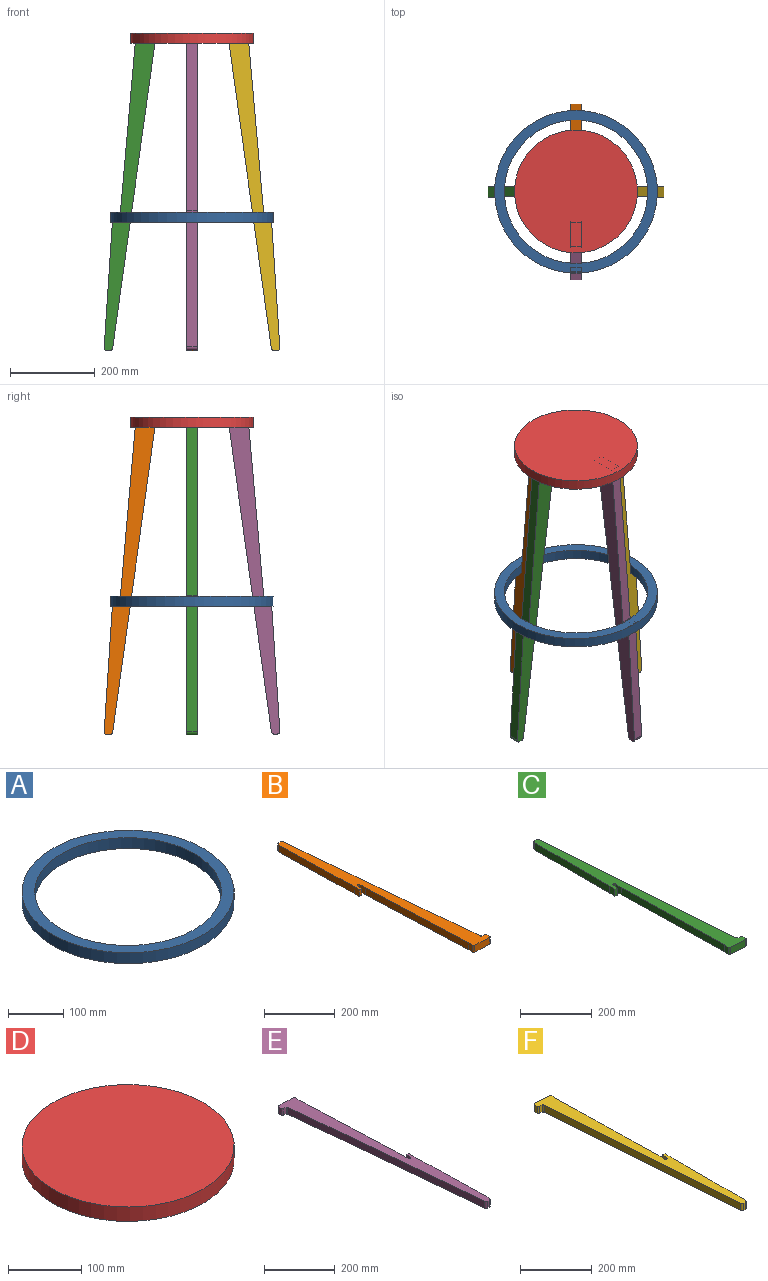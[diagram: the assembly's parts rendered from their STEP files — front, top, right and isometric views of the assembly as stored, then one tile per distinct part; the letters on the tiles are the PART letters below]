
ASSEMBLY  parts=6 mates=7
PART A: 40 faces, bbox 384x384x24 mm
  f0: plane 20x12.69mm, normal (-1,0,0), area 253.7mm2, adj f1,f31,f35,f36
  f1: cylinder r=4mm len=20mm, axis (0,0,-1), area 252.9mm2, adj f0,f2,f35,f36
  f2: plane 20x4.34mm, normal (0,1,0), area 86.9mm2, adj f1,f3,f35,f36
  f3: cylinder r=4mm len=20mm, axis (0,0,-1), area 251.3mm2, adj f2,f4,f35,f36
  f4: plane 20x8mm, normal (1,0,0), area 160mm2, adj f3,f5,f35,f36
  f5: cylinder r=4mm len=20mm, axis (0,0,-1), area 251.3mm2, adj f4,f6,f35,f36
  f6: plane 20x4.34mm, normal (0,-1,0), area 86.9mm2, adj f5,f31,f35,f36
  f7: plane 20x12.69mm, normal (0,-1,0), area 253.7mm2, adj f8,f28,f35,f39
  f8: cylinder r=4mm len=20mm, axis (0,0,-1), area 252.9mm2, adj f7,f9,f35,f39
  f9: plane 20x4.34mm, normal (-1,0,0), area 86.9mm2, adj f8,f10,f35,f39
  f10: cylinder r=4mm len=20mm, axis (0,0,-1), area 251.3mm2, adj f9,f11,f35,f39
  f11: plane 20x8mm, normal (0,1,0), area 160mm2, adj f10,f12,f35,f39
  f12: cylinder r=4mm len=20mm, axis (0,0,-1), area 251.3mm2, adj f11,f13,f35,f39
  f13: plane 20x4.34mm, normal (1,0,0), area 86.9mm2, adj f12,f28,f35,f39
  f14: plane 20x12.69mm, normal (0,1,0), area 253.7mm2, adj f15,f29,f35,f38
  f15: cylinder r=4mm len=20mm, axis (0,0,-1), area 252.9mm2, adj f14,f16,f35,f38
  f16: plane 20x4.34mm, normal (1,0,0), area 86.9mm2, adj f15,f17,f35,f38
  f17: cylinder r=4mm len=20mm, axis (0,0,-1), area 251.3mm2, adj f16,f18,f35,f38
  f18: plane 20x8mm, normal (0,-1,0), area 160mm2, adj f17,f19,f35,f38
  f19: cylinder r=4mm len=20mm, axis (0,0,-1), area 251.3mm2, adj f18,f20,f35,f38
  f20: plane 20x4.34mm, normal (-1,0,0), area 86.9mm2, adj f19,f29,f35,f38
  f21: plane 20x12.69mm, normal (1,0,0), area 253.7mm2, adj f22,f30,f35,f37
  f22: cylinder r=4mm len=20mm, axis (0,0,-1), area 252.9mm2, adj f21,f23,f35,f37
  f23: plane 20x4.34mm, normal (0,-1,0), area 86.9mm2, adj f22,f24,f35,f37
  f24: cylinder r=4mm len=20mm, axis (0,0,-1), area 251.3mm2, adj f23,f25,f35,f37
  f25: plane 20x8mm, normal (-1,0,0), area 160mm2, adj f24,f26,f35,f37
  f26: cylinder r=4mm len=20mm, axis (0,0,-1), area 251.3mm2, adj f25,f27,f35,f37
  f27: plane 20x4.34mm, normal (0,1,0), area 86.9mm2, adj f26,f30,f35,f37
  f28: cylinder r=4mm len=20mm, axis (0,0,-1), area 252.9mm2, adj f7,f13,f35,f39
  f29: cylinder r=4mm len=20mm, axis (0,0,-1), area 252.9mm2, adj f14,f20,f35,f38
  f30: cylinder r=4mm len=20mm, axis (0,0,-1), area 252.9mm2, adj f21,f27,f35,f37
  f31: cylinder r=4mm len=20mm, axis (0,0,-1), area 252.9mm2, adj f0,f6,f35,f36
  f32: cylinder r=169mm len=338mm, axis (0,0,-1), area 25484.6mm2, adj f34,f35
  f33: cylinder r=192mm len=384mm, axis (0,0,-1), area 28952.9mm2, adj f34,f35
  f34: plane 384x384mm, normal (0,0,1), area 26084.6mm2, adj f32,f33
  f35: plane 384x384mm, normal (0,0,-1), area 24847.9mm2, adj f0,f1,f2,f3,f4,f5,f6,f7
  f36: plane 26.4x15.2mm, normal (0,0,-1), area 309.2mm2, adj f0,f1,f2,f3,f4,f5,f6,f31
  f37: plane 26.4x15.2mm, normal (0,0,-1), area 309.2mm2, adj f21,f22,f23,f24,f25,f26,f27,f30
  f38: plane 26.4x15.2mm, normal (0,0,-1), area 309.2mm2, adj f14,f15,f16,f17,f18,f19,f20,f29
  f39: plane 26.4x15.2mm, normal (0,0,-1), area 309.2mm2, adj f7,f8,f9,f10,f11,f12,f13,f28
PART B: 21 faces, bbox 106.4x750.9x24 mm
  f0: plane 24x11.99mm, normal (1,-0.04,0), area 288mm2, adj f1,f18,f19,f20
  f1: cylinder r=4mm len=24mm, axis (0,0,-1), area 150.8mm2, adj f0,f2,f19,f20
  f2: plane 24x10.88mm, normal (0.04,1,0), area 261.3mm2, adj f1,f3,f19,f20
  f3: cylinder r=4mm len=24mm, axis (0,0,-1), area 137.6mm2, adj f2,f4,f19,f20
  f4: plane 720.18x67.82mm, normal (1,0.09,0), area 17360.9mm2, adj f3,f5,f19,f20
  f5: cylinder r=7mm len=24mm, axis (0,0,-1), area 240.7mm2, adj f4,f6,f19,f20
  f6: plane 24x6.09mm, normal (0.04,1,0), area 146.3mm2, adj f5,f7,f19,f20
  f7: cylinder r=7mm len=24mm, axis (0,0,-1), area 274.9mm2, adj f6,f8,f19,f20
  f8: plane 295.62x24mm, normal (-1,-0.02,0), area 7096.5mm2, adj f7,f9,f19,f20
  f9: plane 24x20.98mm, normal (-1,0.04,0), area 504mm2, adj f8,f10,f19,f20
  f10: plane 24x9.99mm, normal (-0.04,-1,0), area 240mm2, adj f9,f11,f19,f20
  f11: plane 24x16.98mm, normal (1,-0.04,0), area 408mm2, adj f10,f12,f19,f20
  f12: cylinder r=4.56mm len=24mm, axis (0,0,-1), area 343.8mm2, adj f11,f13,f19,f20
  f13: plane 24x21.98mm, normal (-1,0.04,0), area 528mm2, adj f12,f14,f19,f20
  f14: plane 398.63x24mm, normal (-1,-0.04,0), area 9576mm2, adj f13,f15,f19,f20
  f15: plane 24x15.98mm, normal (-1,0.04,0), area 384mm2, adj f14,f16,f19,f20
  f16: cylinder r=4mm len=24mm, axis (0,0,-1), area 150.8mm2, adj f15,f17,f19,f20
  f17: plane 56.95x24mm, normal (-0.04,-1,0), area 1368mm2, adj f16,f18,f19,f20
  f18: cylinder r=4mm len=24mm, axis (0,0,-1), area 150.8mm2, adj f0,f17,f19,f20
  f19: plane 750.88x106.39mm, normal (0,0,1), area 25896.7mm2, adj f0,f1,f2,f3,f4,f5,f6,f7
  f20: plane 750.88x106.39mm, normal (0,0,-1), area 25896.7mm2, adj f0,f1,f2,f3,f4,f5,f6,f7
PART C: 21 faces, bbox 92x752.8x24 mm
  f0: cylinder r=4mm len=24mm, axis (0,0,-1), area 150.8mm2, adj f1,f18,f19,f20
  f1: plane 24x10.86mm, normal (0.07,1,0), area 261.3mm2, adj f0,f2,f19,f20
  f2: cylinder r=4mm len=24mm, axis (0,0,-1), area 137.6mm2, adj f1,f3,f19,f20
  f3: plane 721.48x52.22mm, normal (1,0.07,0), area 17360.9mm2, adj f2,f4,f19,f20
  f4: cylinder r=7mm len=24mm, axis (0,0,-1), area 240.7mm2, adj f3,f5,f19,f20
  f5: plane 24x6.08mm, normal (0.07,1,0), area 146.3mm2, adj f4,f6,f19,f20
  f6: cylinder r=7mm len=24mm, axis (0,0,-1), area 274.9mm2, adj f5,f7,f19,f20
  f7: plane 295.69x24mm, normal (-1,0,0), area 7096.5mm2, adj f6,f8,f19,f20
  f8: plane 24x20.95mm, normal (-1,0.07,0), area 504mm2, adj f7,f9,f19,f20
  f9: plane 24x9.98mm, normal (-0.07,-1,0), area 240mm2, adj f8,f10,f19,f20
  f10: plane 24x16.96mm, normal (1,-0.07,0), area 408mm2, adj f9,f11,f19,f20
  f11: cylinder r=4.56mm len=24mm, axis (0,0,-1), area 343.8mm2, adj f10,f12,f19,f20
  f12: plane 24x21.95mm, normal (-1,0.07,0), area 528mm2, adj f11,f13,f19,f20
  f13: plane 398.91x24mm, normal (-1,-0.02,0), area 9576mm2, adj f12,f14,f19,f20
  f14: plane 24x15.97mm, normal (-1,0.07,0), area 384mm2, adj f13,f15,f19,f20
  f15: cylinder r=4mm len=24mm, axis (0,0,-1), area 150.8mm2, adj f14,f16,f19,f20
  f16: plane 56.88x24mm, normal (-0.07,-1,0), area 1368mm2, adj f15,f17,f19,f20
  f17: cylinder r=4mm len=24mm, axis (0,0,-1), area 150.8mm2, adj f16,f18,f19,f20
  f18: plane 24x11.97mm, normal (1,-0.07,0), area 288mm2, adj f0,f17,f19,f20
  f19: plane 752.76x91.99mm, normal (0,0,1), area 25896.7mm2, adj f0,f1,f2,f3,f4,f5,f6,f7
  f20: plane 752.76x91.99mm, normal (0,0,-1), area 25896.7mm2, adj f0,f1,f2,f3,f4,f5,f6,f7
PART D: 39 faces, bbox 290x290x24 mm
  f0: cylinder r=4mm len=20mm, axis (0,0,-1), area 252.9mm2, adj f1,f31,f34,f35
  f1: plane 20x12.69mm, normal (0,1,0), area 253.7mm2, adj f0,f2,f34,f35
  f2: cylinder r=4mm len=20mm, axis (0,0,-1), area 252.9mm2, adj f1,f3,f34,f35
  f3: plane 53.69x20mm, normal (1,0,0), area 1073.7mm2, adj f2,f4,f34,f35
  f4: cylinder r=4mm len=20mm, axis (0,0,-1), area 252.9mm2, adj f3,f5,f34,f35
  f5: plane 20x12.69mm, normal (0,-1,0), area 253.7mm2, adj f4,f6,f34,f35
  f6: cylinder r=4mm len=20mm, axis (0,0,-1), area 252.9mm2, adj f5,f31,f34,f35
  f7: plane 20x12.69mm, normal (0,-1,0), area 253.7mm2, adj f8,f28,f34,f38
  f8: cylinder r=4mm len=20mm, axis (0,0,-1), area 252.9mm2, adj f7,f9,f34,f38
  f9: plane 53.69x20mm, normal (-1,0,0), area 1073.7mm2, adj f8,f10,f34,f38
  f10: cylinder r=4mm len=20mm, axis (0,0,-1), area 252.9mm2, adj f9,f11,f34,f38
  f11: plane 20x12.69mm, normal (0,1,0), area 253.7mm2, adj f10,f12,f34,f38
  f12: cylinder r=4mm len=20mm, axis (0,0,-1), area 252.9mm2, adj f11,f13,f34,f38
  f13: plane 53.69x20mm, normal (1,0,0), area 1073.7mm2, adj f12,f28,f34,f38
  f14: plane 53.69x20mm, normal (0,-1,0), area 1073.7mm2, adj f15,f29,f34,f37
  f15: cylinder r=4mm len=20mm, axis (0,0,-1), area 252.9mm2, adj f14,f16,f34,f37
  f16: plane 20x12.69mm, normal (-1,0,0), area 253.7mm2, adj f15,f17,f34,f37
  f17: cylinder r=4mm len=20mm, axis (0,0,-1), area 252.9mm2, adj f16,f18,f34,f37
  f18: plane 53.69x20mm, normal (0,1,0), area 1073.7mm2, adj f17,f19,f34,f37
  f19: cylinder r=4mm len=20mm, axis (0,0,-1), area 252.9mm2, adj f18,f20,f34,f37
  f20: plane 20x12.69mm, normal (1,0,0), area 253.7mm2, adj f19,f29,f34,f37
  f21: plane 20x12.69mm, normal (-1,0,0), area 253.7mm2, adj f22,f30,f34,f36
  f22: cylinder r=4mm len=20mm, axis (0,0,-1), area 252.9mm2, adj f21,f23,f34,f36
  f23: plane 53.69x20mm, normal (0,1,0), area 1073.7mm2, adj f22,f24,f34,f36
  f24: cylinder r=4mm len=20mm, axis (0,0,-1), area 252.9mm2, adj f23,f25,f34,f36
  f25: plane 20x12.69mm, normal (1,0,0), area 253.7mm2, adj f24,f26,f34,f36
  f26: cylinder r=4mm len=20mm, axis (0,0,-1), area 252.9mm2, adj f25,f27,f34,f36
  f27: plane 53.69x20mm, normal (0,-1,0), area 1073.7mm2, adj f26,f30,f34,f36
  f28: cylinder r=4mm len=20mm, axis (0,0,-1), area 252.9mm2, adj f7,f13,f34,f38
  f29: cylinder r=4mm len=20mm, axis (0,0,-1), area 252.9mm2, adj f14,f20,f34,f37
  f30: cylinder r=4mm len=20mm, axis (0,0,-1), area 252.9mm2, adj f21,f27,f34,f36
  f31: plane 53.69x20mm, normal (-1,0,0), area 1073.7mm2, adj f0,f6,f34,f35
  f32: cylinder r=145mm len=290mm, axis (0,0,-1), area 21865.5mm2, adj f33,f34
  f33: plane 290x290mm, normal (0,0,1), area 66052mm2, adj f32
  f34: plane 290x290mm, normal (0,0,-1), area 59660.7mm2, adj f0,f1,f2,f3,f4,f5,f6,f7
  f35: plane 67.4x26.4mm, normal (0,0,-1), area 1597.8mm2, adj f0,f1,f2,f3,f4,f5,f6,f31
  f36: plane 67.4x26.4mm, normal (0,0,-1), area 1597.8mm2, adj f21,f22,f23,f24,f25,f26,f27,f30
  f37: plane 67.4x26.4mm, normal (0,0,-1), area 1597.8mm2, adj f14,f15,f16,f17,f18,f19,f20,f29
  f38: plane 67.4x26.4mm, normal (0,0,-1), area 1597.8mm2, adj f7,f8,f9,f10,f11,f12,f13,f28
PART E: 21 faces, bbox 106.4x750.9x24 mm
  f0: plane 24x11.99mm, normal (-1,0.04,0), area 288mm2, adj f1,f18,f19,f20
  f1: cylinder r=4mm len=24mm, axis (0,0,-1), area 150.8mm2, adj f0,f2,f19,f20
  f2: plane 24x10.88mm, normal (-0.04,-1,0), area 261.3mm2, adj f1,f3,f19,f20
  f3: cylinder r=4mm len=24mm, axis (0,0,-1), area 137.6mm2, adj f2,f4,f19,f20
  f4: plane 720.18x67.82mm, normal (-1,-0.09,0), area 17360.9mm2, adj f3,f5,f19,f20
  f5: cylinder r=7mm len=24mm, axis (0,0,-1), area 240.7mm2, adj f4,f6,f19,f20
  f6: plane 24x6.09mm, normal (-0.04,-1,0), area 146.3mm2, adj f5,f7,f19,f20
  f7: cylinder r=7mm len=24mm, axis (0,0,-1), area 274.9mm2, adj f6,f8,f19,f20
  f8: plane 295.62x24mm, normal (1,0.02,0), area 7096.5mm2, adj f7,f9,f19,f20
  f9: plane 24x20.98mm, normal (1,-0.04,0), area 504mm2, adj f8,f10,f19,f20
  f10: plane 24x9.99mm, normal (0.04,1,0), area 240mm2, adj f9,f11,f19,f20
  f11: plane 24x16.98mm, normal (-1,0.04,0), area 408mm2, adj f10,f12,f19,f20
  f12: cylinder r=4.56mm len=24mm, axis (0,0,-1), area 343.8mm2, adj f11,f13,f19,f20
  f13: plane 24x21.98mm, normal (1,-0.04,0), area 528mm2, adj f12,f14,f19,f20
  f14: plane 398.63x24mm, normal (1,0.04,0), area 9576mm2, adj f13,f15,f19,f20
  f15: plane 24x15.98mm, normal (1,-0.04,0), area 384mm2, adj f14,f16,f19,f20
  f16: cylinder r=4mm len=24mm, axis (0,0,-1), area 150.8mm2, adj f15,f17,f19,f20
  f17: plane 56.95x24mm, normal (0.04,1,0), area 1368mm2, adj f16,f18,f19,f20
  f18: cylinder r=4mm len=24mm, axis (0,0,-1), area 150.8mm2, adj f0,f17,f19,f20
  f19: plane 750.88x106.39mm, normal (0,0,1), area 25896.7mm2, adj f0,f1,f2,f3,f4,f5,f6,f7
  f20: plane 750.88x106.39mm, normal (0,0,-1), area 25896.7mm2, adj f0,f1,f2,f3,f4,f5,f6,f7
PART F: 21 faces, bbox 92x752.8x24 mm
  f0: plane 24x10.86mm, normal (-0.07,-1,0), area 261.3mm2, adj f1,f18,f19,f20
  f1: cylinder r=4mm len=24mm, axis (0,0,-1), area 137.6mm2, adj f0,f2,f19,f20
  f2: plane 721.48x52.22mm, normal (-1,-0.07,0), area 17360.9mm2, adj f1,f3,f19,f20
  f3: cylinder r=7mm len=24mm, axis (0,0,-1), area 240.7mm2, adj f2,f4,f19,f20
  f4: plane 24x6.08mm, normal (-0.07,-1,0), area 146.3mm2, adj f3,f5,f19,f20
  f5: cylinder r=7mm len=24mm, axis (0,0,-1), area 274.9mm2, adj f4,f6,f19,f20
  f6: plane 295.69x24mm, normal (1,0,0), area 7096.5mm2, adj f5,f7,f19,f20
  f7: plane 24x20.95mm, normal (1,-0.07,0), area 504mm2, adj f6,f8,f19,f20
  f8: plane 24x9.98mm, normal (0.07,1,0), area 240mm2, adj f7,f9,f19,f20
  f9: plane 24x16.96mm, normal (-1,0.07,0), area 408mm2, adj f8,f10,f19,f20
  f10: cylinder r=4.56mm len=24mm, axis (0,0,-1), area 343.8mm2, adj f9,f11,f19,f20
  f11: plane 24x21.95mm, normal (1,-0.07,0), area 528mm2, adj f10,f12,f19,f20
  f12: plane 398.91x24mm, normal (1,0.02,0), area 9576mm2, adj f11,f13,f19,f20
  f13: plane 24x15.97mm, normal (1,-0.07,0), area 384mm2, adj f12,f14,f19,f20
  f14: cylinder r=4mm len=24mm, axis (0,0,-1), area 150.8mm2, adj f13,f15,f19,f20
  f15: plane 56.88x24mm, normal (0.07,1,0), area 1368mm2, adj f14,f16,f19,f20
  f16: cylinder r=4mm len=24mm, axis (0,0,-1), area 150.8mm2, adj f15,f17,f19,f20
  f17: plane 24x11.97mm, normal (-1,0.07,0), area 288mm2, adj f16,f18,f19,f20
  f18: cylinder r=4mm len=24mm, axis (0,0,-1), area 150.8mm2, adj f0,f17,f19,f20
  f19: plane 752.76x91.99mm, normal (0,0,1), area 25896.7mm2, adj f0,f1,f2,f3,f4,f5,f6,f7
  f20: plane 752.76x91.99mm, normal (0,0,-1), area 25896.7mm2, adj f0,f1,f2,f3,f4,f5,f6,f7
PLACE A rot(axis=(0,0,1),90deg) t=(-319.28,1406.31,33.52)mm
PLACE B rot(axis=(-0.57,0.59,-0.57),118.6deg) t=(-928.28,-1561.08,7.78)mm
PLACE C rot(axis=(-1,0.03,0.03),90.1deg) t=(380.16,-166.69,-8.66)mm
PLACE D t=(644.72,-751.69,455.99)mm fixed
PLACE E rot(axis=(0.57,-0.59,-0.57),118.6deg) t=(-904.28,-1820.88,162.2)mm
PLACE F rot(axis=(1,-0.03,0.03),90.1deg) t=(640.24,-142.69,174.64)mm
MATE cylindrical D.f32 <-> A.f32  axis (0,0,1) through (-916.28,-154.69,479.99)mm
MATE parallel E.f15 <-> D.f11  axis (0,-1,0) through (-916.28,-288.69,465.99)mm
MATE parallel E.f20 <-> D.f9  axis (1,0,0) through (-904.28,-303.07,145.07)mm
MATE fastened F.f15 <-> D.f37  axis (0,0,1) through (-814.78,-154.69,475.99)mm
MATE parallel A.f20 <-> F.f20  axis (0,-1,0) through (-736.61,-142.69,43.52)mm
MATE fastened B.f17 <-> D.f35  axis (0,0,1) through (-916.28,-53.19,475.99)mm
MATE fastened C.f16 <-> D.f36  axis (0,0,1) through (-1017.78,-154.69,475.99)mm
